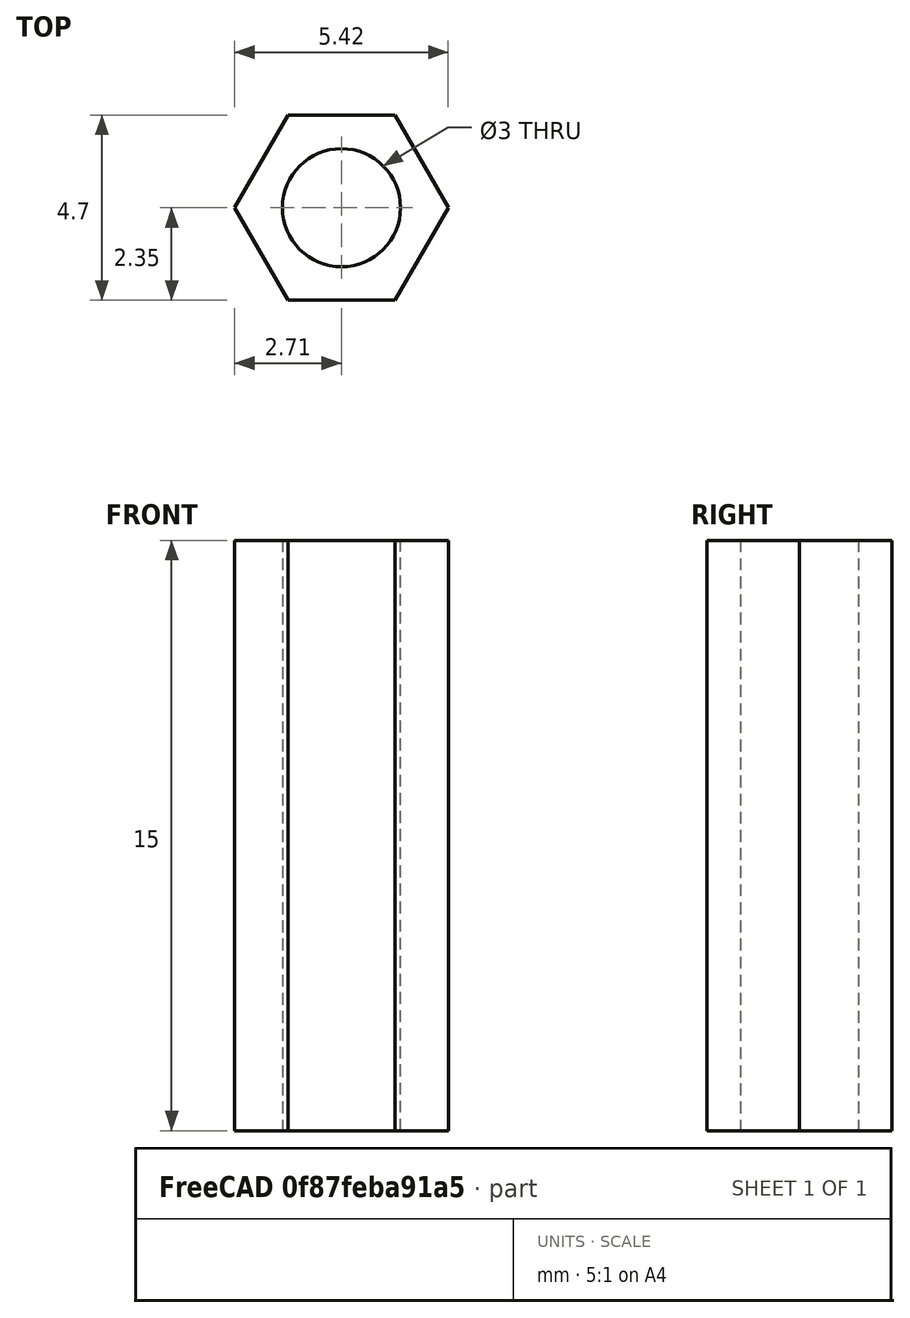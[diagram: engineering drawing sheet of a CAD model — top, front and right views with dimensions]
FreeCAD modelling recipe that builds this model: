
FCSTD DOCUMENT  (FreeCAD 0.18.4R)
Label: coxial_M3_15mm
License: All rights reserved
LicenseURL: http://en.wikipedia.org/wiki/All_rights_reserved
objects: Sketcher::SketchObject×1, PartDesign::Pad×1, PartDesign::Body×1
note: 4 computed .brp shape members not serialized (recipe doc carries the construction recipe); baked Part::Feature solids carry a one-line shape summary decoded from their .brp

FEATURE [Sketcher::SketchObject] Sketch
  MapMode = 5
  Support = -> [XY_Plane]
  sketch-geometry (8):
    g0: Circle CenterX=0 CenterY=0 CenterZ=0 NormalX=0 NormalY=0 NormalZ=1 AngleXU=0 Radius=1.5
    g1: LineSegment StartX=1.35677 StartY=-2.35 StartZ=0 EndX=2.71355 EndY=1.24363e-11 EndZ=0
    g2: LineSegment StartX=2.71355 StartY=1.24363e-11 StartZ=0 EndX=1.35677 EndY=2.35 EndZ=0
    g3: LineSegment StartX=1.35677 StartY=2.35 StartZ=0 EndX=-1.35677 EndY=2.35 EndZ=0
    g4: LineSegment StartX=-1.35677 StartY=2.35 StartZ=0 EndX=-2.71355 EndY=-9.1513e-12 EndZ=0
    g5: LineSegment StartX=-2.71355 StartY=-9.1513e-12 StartZ=0 EndX=-1.35677 EndY=-2.35 EndZ=0
    g6: LineSegment StartX=-1.35677 StartY=-2.35 StartZ=0 EndX=1.35677 EndY=-2.35 EndZ=0
    g7: Circle [constr] CenterX=0 CenterY=0 CenterZ=0 NormalX=0 NormalY=0 NormalZ=1 AngleXU=0 Radius=2.71355
  constraints (18):
    c: Coincident(g0,g-1)
    c: Radius(g0) = 1.5
    c: Coincident(g1,g2)
    c: Coincident(g2,g3)
    c: Coincident(g3,g4)
    c: Coincident(g4,g5)
    c: Coincident(g5,g6)
    c: Coincident(g6,g1)
    c: Equal(g1, g2-g6) x5
    c: PointOnObject(g1,g7)
    c: PointOnObject(g2,g7)
    c: PointOnObject(g3,g7)
    c: PointOnObject(g4,g7)
    c: PointOnObject(g5,g7)
    c: PointOnObject(g6,g7)
    c: Distance(g2,g4) = 4.7
    c: Coincident(g7,g0)
    c: Horizontal(g3)
FEATURE [PartDesign::Pad] Pad
  Length = 15
  Length2 = 100
  Profile = -> Sketch
  Type = 0
FEATURE [PartDesign::Body] Body
  Group = -> [Sketch,Pad]
  Origin = -> Origin
  Tip = -> Pad
